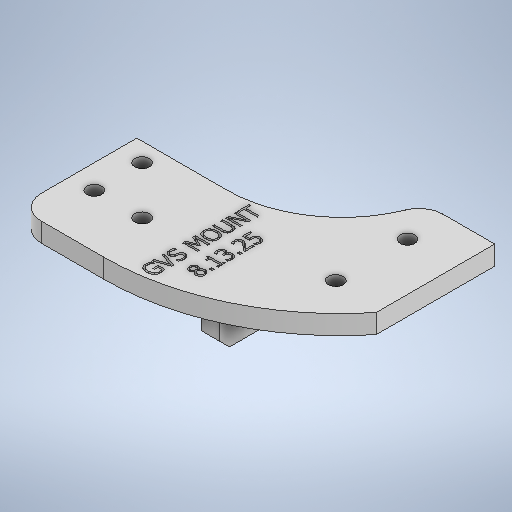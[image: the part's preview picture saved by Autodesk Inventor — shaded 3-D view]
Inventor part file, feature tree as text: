
AUTODESK INVENTOR PART (.ipt)
format: ipt  version: 2025 (Build 290162000, 162)  size: 679,424 bytes
history: native  units: mm
features: sketch x6, fillet x3, extrude x2, chamfer x2, emboss x1
ambient origin geometry x8: Origin, YZ Plane, XZ Plane, XY Plane, X Axis, Y Axis, Z Axis, Center Point
bodies: Solid1 (feature_tree)
feature tree (14):
  extrude  "Extrusion1"  Depth=3.9mm
  fillet  "Fillet2"  Radius=25.0mm
  emboss  "Emboss1"
  extrude  "Extrusion3"  Depth=56.58mm
  fillet  "Fillet3"  Radius=3.1mm
  chamfer  "Chamfer1"  Distance=20.0mm
  chamfer  "Chamfer2"  Distance=4.0mm
  fillet  "Fillet4"  Radius=5.0mm
  sketch  "Sketch1"  dims[d0=3.1mm d1=3.9mm]
  sketch  "Sketch Rectangular Pattern1"  dims[d2=20.0mm d4=10.0mm d5=10.0mm d7=10.0mm]
  sketch  "Sketch Rectangular Pattern2"  dims[d9=20.0mm d11=10.0mm d12=10.0mm d14=10.0mm d16=25.0mm]
  sketch  "Sketch Rectangular Pattern3"  dims[d17=5.0mm d18=56.58mm d19=3.1mm]
  sketch  "Sketch3"  dims[d20=10.0mm]
  sketch  "Sketch4"  dims[d21=20.0mm d23=15.0mm d24=10.0mm d26=10.0mm d28=20.0mm d29=4.0mm d30=0.0mm d38=5.0mm d39=1.0mm d40=0.0mm d41=5.0mm d42=10.1mm d43=2.0mm d44=2.0mm d45=7.0mm d46=0.0mm d47=2.0mm d48=2.0mm d49=2.0mm d50=45.0deg d51=5.0mm d52=2.0mm d53=45.0deg d54=3.0mm]
